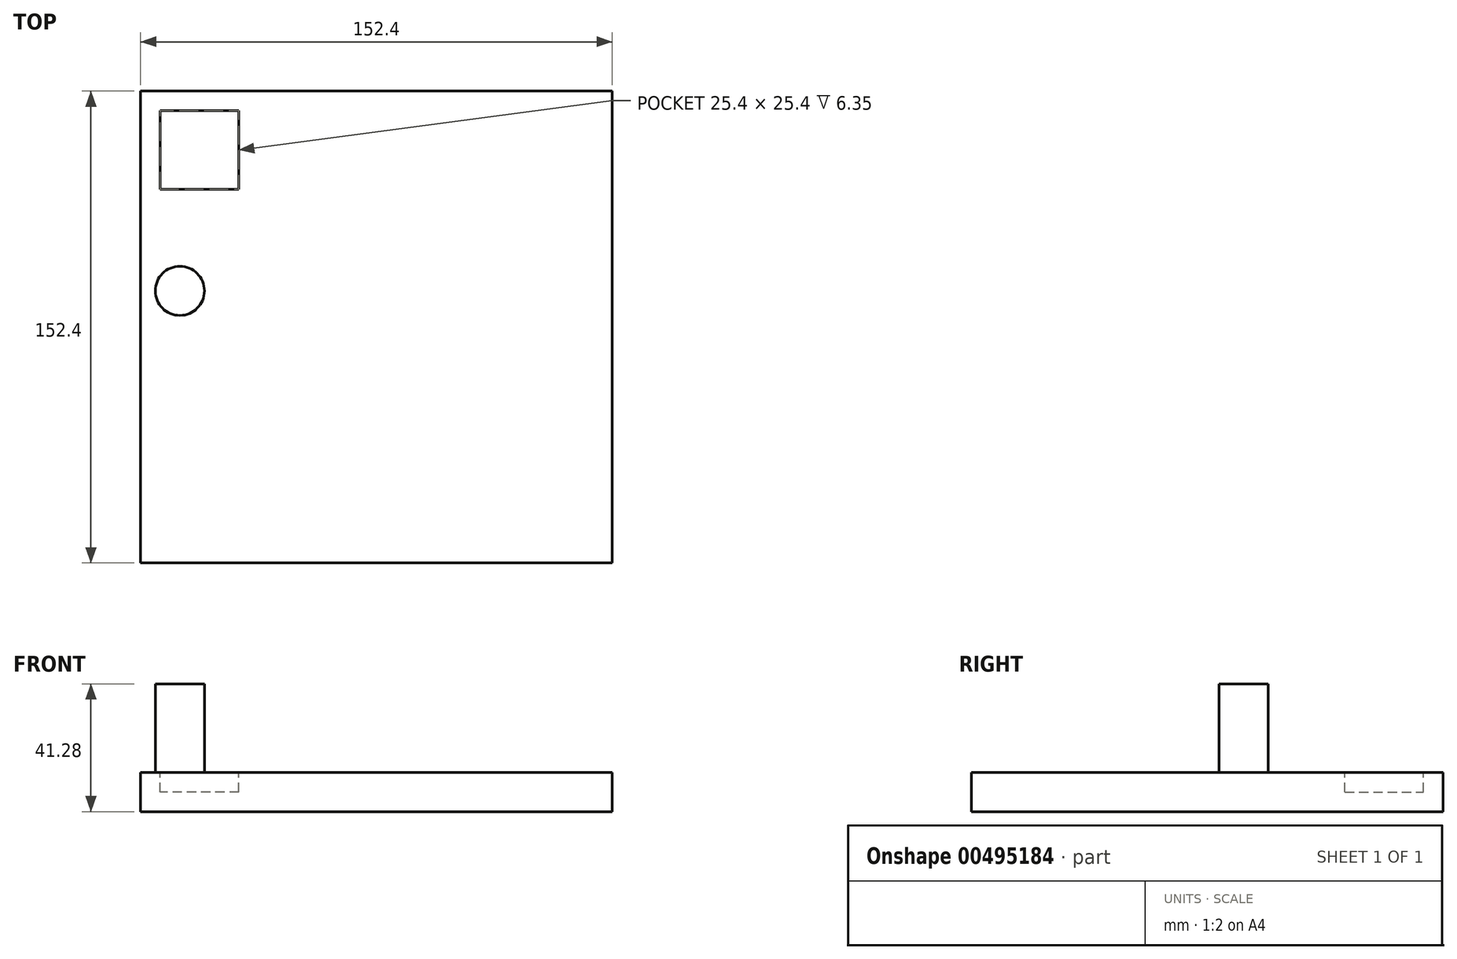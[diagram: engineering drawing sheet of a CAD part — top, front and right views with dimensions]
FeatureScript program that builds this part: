
annotation { "Feature Type Name" : "Feature", "Feature Type Description" : "" }
export const myFeature = defineFeature(function(context is Context, id is Id, definition is map)
    precondition{}
    {
        {
            var Q0;
            Q0=qCreatedBy(makeId("Top.planeOp"),FACE);
            var sketch = newSketch(context, id + "F0", { "sketchPlane" : qUnion([Q0])});
            skLineSegment(sketch, "E0.bottom", {"start": v(76.2, 76.2) * mm, "end": v(-76.2, 76.2) * mm});
            skLineSegment(sketch, "E0.top", {"start": v(76.2, -76.2) * mm, "end": v(-76.2, -76.2) * mm});
            skLineSegment(sketch, "E0.left", {"start": v(76.2, 76.2) * mm, "end": v(76.2, -76.2) * mm});
            skLineSegment(sketch, "E0.right", {"start": v(-76.2, 76.2) * mm, "end": v(-76.2, -76.2) * mm});
            skPoint(sketch, "E0.middle", {"position": v(0, 0) * mm});
            skSolve(sketch);
        }
        {
            var Q0;
            Q0 = qSketchRegion(id + "F0", true);
            extrude(context, id + "F1", {"entities" : qUnion([Q0]), "endBound" : BoundingType.SYMMETRIC, "depth" : 12.7 * mm});
        }
        {
            var Q0;
            Q0=makeQuery(id+"F1.opExtrude","CAP_FACE",FACE,{"disambiguationData":[OSD([sQuery(id+"F0.wireOp",EDGE,"E0.bottom"),sQuery(id+"F0.wireOp",EDGE,"E0.top"),sQuery(id+"F0.wireOp",EDGE,"E0.left"),sQuery(id+"F0.wireOp",EDGE,"E0.right")])],"isStart":false});
            var sketch = newSketch(context, id + "F2", { "sketchPlane" : qUnion([Q0])});
            skLineSegment(sketch, "E1.bottom", {"start": v(-44.45, 44.45) * mm, "end": v(-69.85, 44.45) * mm});
            skLineSegment(sketch, "E1.top", {"start": v(-44.45, 69.85) * mm, "end": v(-69.85, 69.85) * mm});
            skLineSegment(sketch, "E1.left", {"start": v(-44.45, 44.45) * mm, "end": v(-44.45, 69.85) * mm});
            skLineSegment(sketch, "E1.right", {"start": v(-69.85, 44.45) * mm, "end": v(-69.85, 69.85) * mm});
            skPoint(sketch, "E1.middle", {"position": v(-57.15, 57.15) * mm});
            skSolve(sketch);
        }
        {
            var Q0;
            Q0 = qSketchRegion(id + "F2", true);
            extrude(context, id + "F3", {"entities" : qUnion([Q0]), "operationType" : NewBodyOperationType.REMOVE, "oppositeDirection" : true, "depth" : 6.35 * mm});
        }
        {
            var Q0;
            Q0=qCreatedBy(makeId("Right.planeOp"),FACE);
            cPlane(context, id + "F4", {"entities" : qUnion([Q0]), "cplaneType" : CPlaneType.OFFSET, "offset" : 63.5 * mm, "oppositeDirection" : true, "width" : 152.4 * mm, "height" : 152.4 * mm});
        }
        {
            var Q0;
            Q0=qCreatedBy(id+"F4.planeOp",FACE);
            var sketch = newSketch(context, id + "F5", { "sketchPlane" : qUnion([Q0])});
            skLineSegment(sketch, "E2.bottom", {"start": v(11.7, 6.35) * mm, "end": v(19.65, 6.35) * mm});
            skLineSegment(sketch, "E2.top", {"start": v(11.7, 34.92) * mm, "end": v(19.65, 34.92) * mm});
            skLineSegment(sketch, "E2.left", {"start": v(11.7, 6.35) * mm, "end": v(11.7, 34.92) * mm});
            skLineSegment(sketch, "E2.right", {"start": v(19.65, 6.35) * mm, "end": v(19.65, 34.93) * mm});
            skPoint(sketch, "E2.middle", {"position": v(15.68, 20.64) * mm});
            skSolve(sketch);
        }
        {
            var Q0;
            Q0=makeQuery(id+"F5.imprint","IMPRINT",FACE,{"disambiguationData":[TD([[makeQuery(id+"F5.imprint","IMPRINT",EDGE,{"derivedFrom":sQuery(id+"F5.wireOp",EDGE,"E2.bottom")}),1.0]])]});
            var Q1;
            Q1=sQuery(id+"F5.wireOp",EDGE,"E2.left");
            revolve(context, id + "F6", {"operationType" : NewBodyOperationType.ADD, "entities" : qUnion([Q0]), "axis" : qUnion([Q1]), "revolveType" : RevolveType.FULL});
        }
    });
